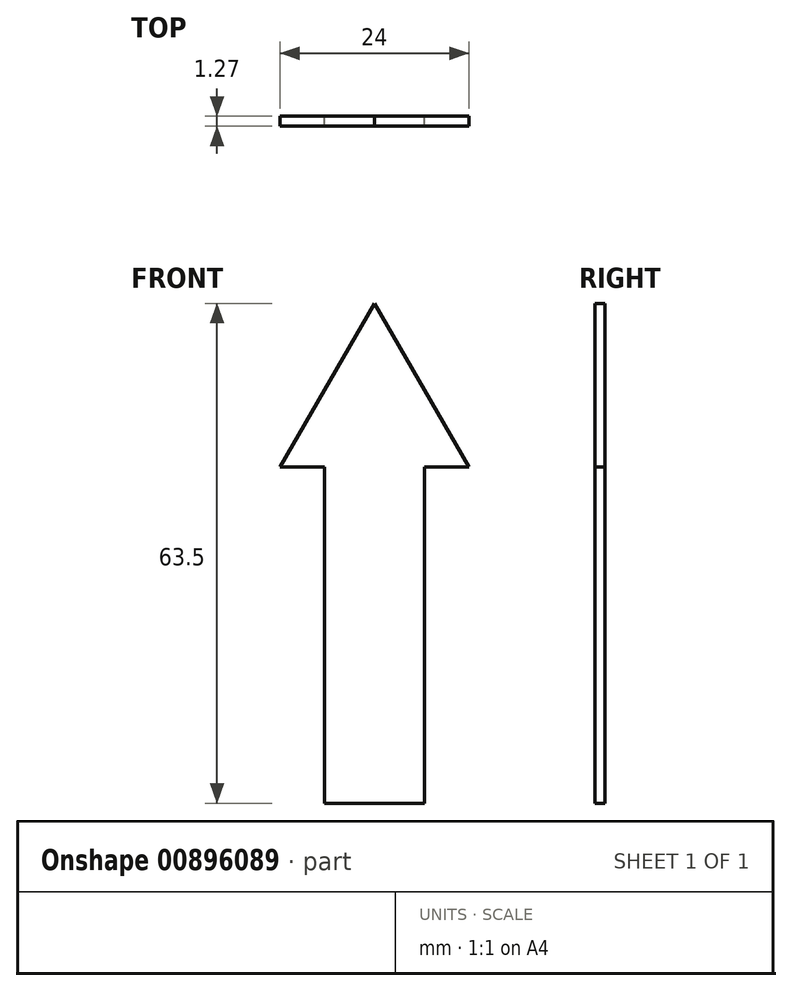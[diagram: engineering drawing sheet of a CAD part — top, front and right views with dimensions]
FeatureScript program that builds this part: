
annotation { "Feature Type Name" : "Feature", "Feature Type Description" : "" }
export const myFeature = defineFeature(function(context is Context, id is Id, definition is map)
    precondition{}
    {
        {
            var Q0;
            Q0=qCreatedBy(makeId("Front.planeOp"),FACE);
            var sketch = newSketch(context, id + "F0", { "sketchPlane" : qUnion([Q0])});
            skLineSegment(sketch, "E0", {"start": v(-6.35, -42.72) * mm, "end": v(6.35, -42.72) * mm});
            skLineSegment(sketch, "E1", {"start": v(6.35, -42.72) * mm, "end": v(6.35, 0) * mm});
            skLineSegment(sketch, "E2", {"start": v(6.35, 0) * mm, "end": v(12, 0) * mm});
            skLineSegment(sketch, "E3", {"start": v(12, 0) * mm, "end": v(0, 20.78) * mm});
            skLineSegment(sketch, "E4", {"start": v(0, 20.78) * mm, "end": v(-12, 0) * mm});
            skLineSegment(sketch, "E5", {"start": v(-12, 0) * mm, "end": v(-6.35, 0) * mm});
            skLineSegment(sketch, "E6", {"start": v(-6.35, 0) * mm, "end": v(-6.35, -42.72) * mm});
            skSolve(sketch);
        }
        {
            var Q0;
            Q0=makeQuery(id+"F0.imprint","IMPRINT",FACE,{"disambiguationData":[TD([[makeQuery(id+"F0.imprint","IMPRINT",EDGE,{"derivedFrom":sQuery(id+"F0.wireOp",EDGE,"E0")}),1.0]])]});
            extrude(context, id + "F1", {"entities" : qUnion([Q0]), "depth" : 1.27 * mm, "offsetDistance" : 25.4 * mm});
        }
    });
